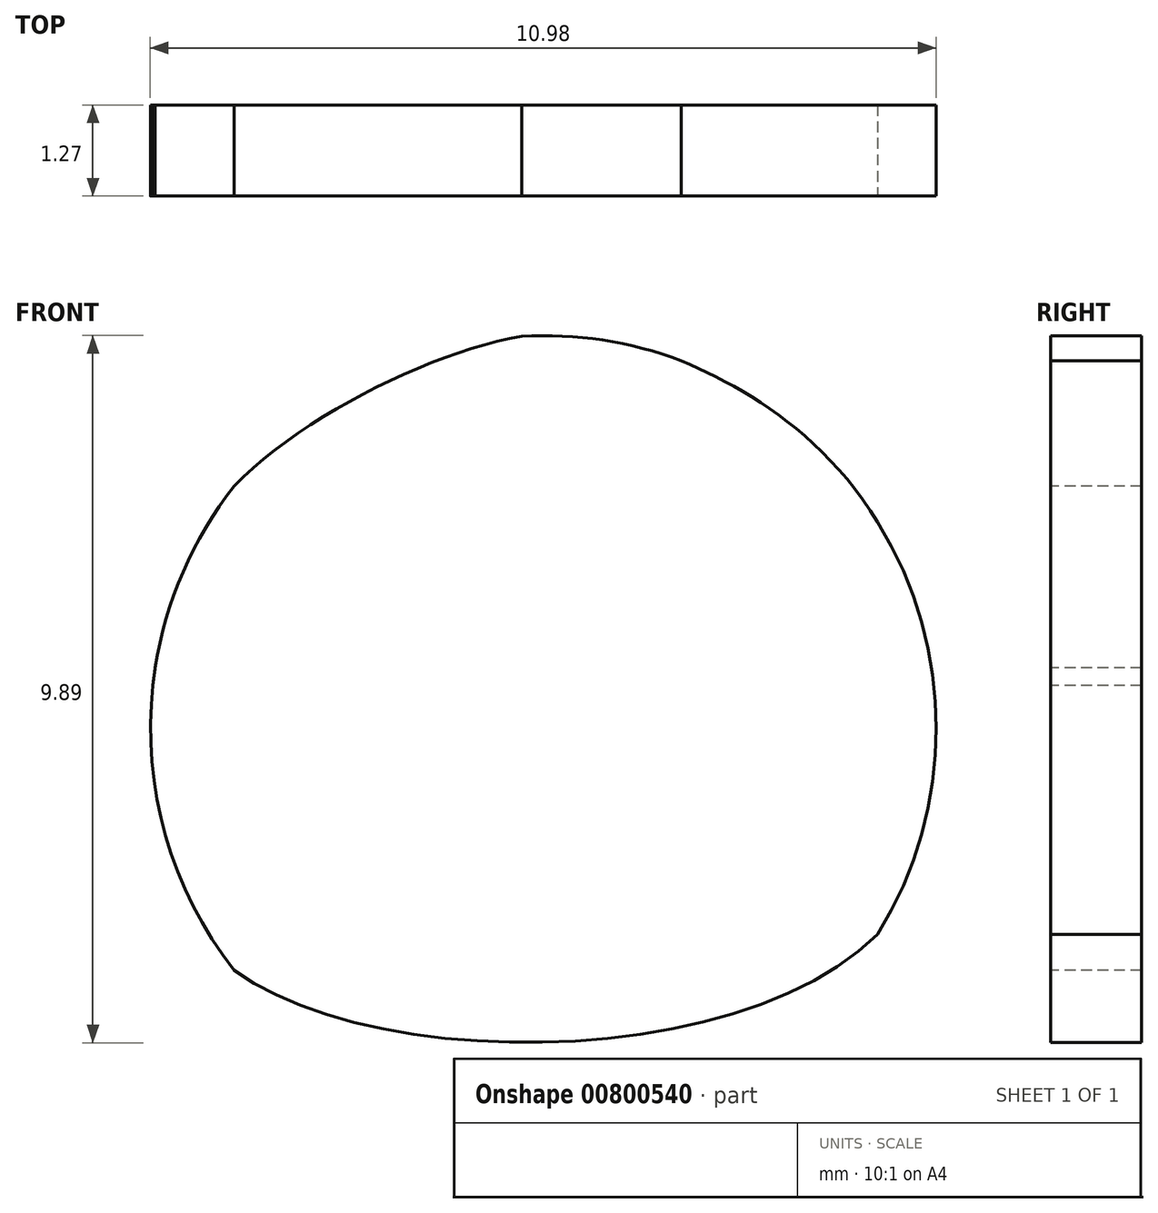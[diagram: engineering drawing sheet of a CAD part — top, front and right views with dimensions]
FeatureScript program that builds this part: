
annotation { "Feature Type Name" : "Feature", "Feature Type Description" : "" }
export const myFeature = defineFeature(function(context is Context, id is Id, definition is map)
    precondition{}
    {
        {
            var Q0;
            Q0=qCreatedBy(makeId("Front.planeOp"),FACE);
            var sketch = newSketch(context, id + "F0", { "sketchPlane" : qUnion([Q0])});
            skArc(sketch, "E0", {"start": v(-31.17, 34.08) * mm, "mid": v(-36.14, 42.45) * mm, "end": v(-40.16, 33.58) * mm});
            skFitSpline(sketch, "E1", {"points": [v(-40.16, 33.58) * mm, v(-31.17, 34.08) * mm, v(-31.17, 39.85) * mm, v(-33.9, 42.1) * mm, v(-36.14, 42.45) * mm, v(-40.16, 40.35) * mm, v(-41.3, 37.57) * mm, v(-40.16, 33.58) * mm]});
            skSolve(sketch);
        }
        {
            var Q0;
            {var subQ0=sQuery(id+"F0.wireOp",EDGE,"E1");var subQ1=sQuery(id+"F0.wireOp",EDGE,"E0");var subQ9=makeQuery(id+"F0.imprint","INTERSECT",VERTEX,{"disambiguationData":[OD(0.0)],"derivedFrom":[subQ1,subQ0]});Q0=makeQuery(id+"F0.imprint","IMPRINT",FACE,{"disambiguationData":[TD([[makeQuery(id+"F0.imprint","IMPRINT",EDGE,{"disambiguationData":[TD([[subQ9,-1.0]])],"derivedFrom":subQ1}),1.0]])]});}
            extrude(context, id + "F1", {"entities" : qUnion([Q0]), "oppositeDirection" : true, "depth" : 1.27 * mm, "offsetDistance" : 25.4 * mm});
        }
    });
